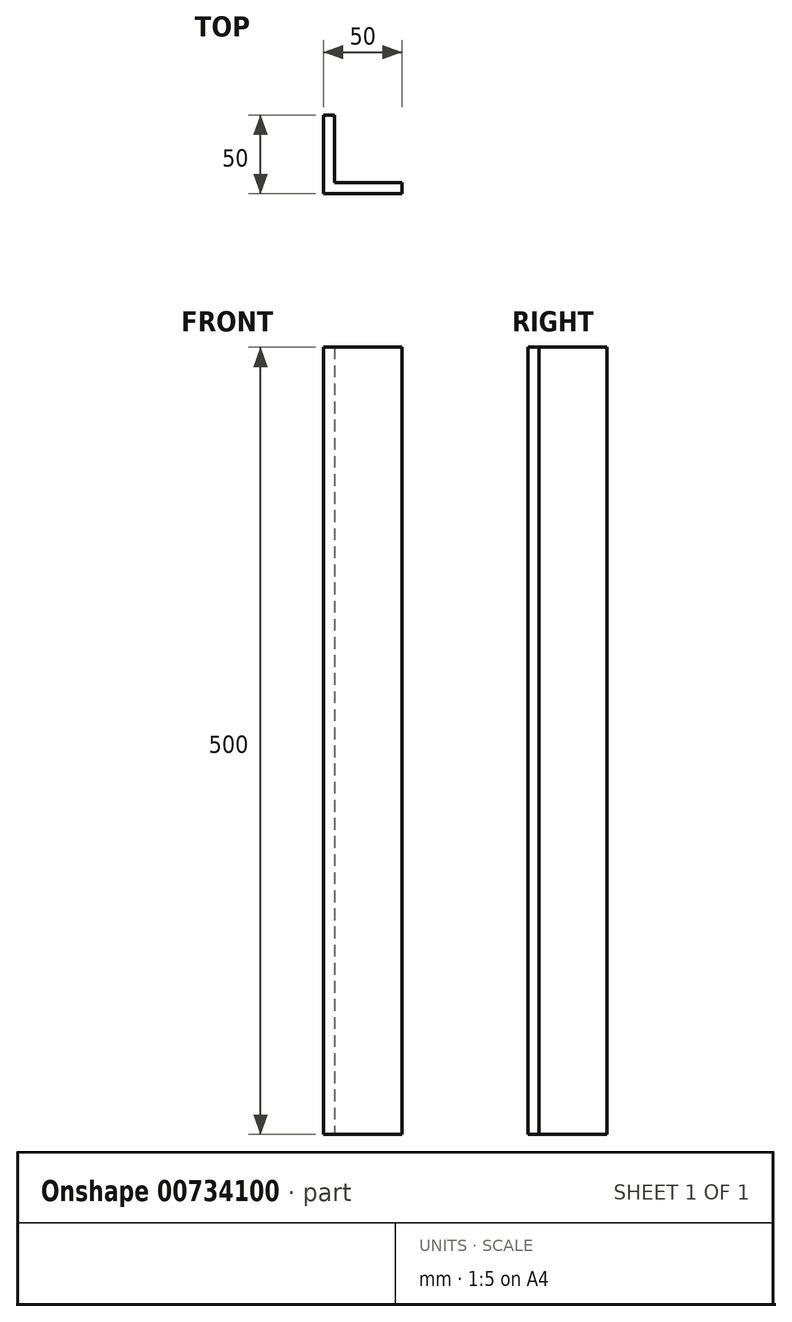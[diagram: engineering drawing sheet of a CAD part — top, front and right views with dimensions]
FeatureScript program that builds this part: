
annotation { "Feature Type Name" : "Feature", "Feature Type Description" : "" }
export const myFeature = defineFeature(function(context is Context, id is Id, definition is map)
    precondition{}
    {
        {
            var Q0;
            Q0=qCreatedBy(makeId("Top.planeOp"),FACE);
            var sketch = newSketch(context, id + "F0", { "sketchPlane" : qUnion([Q0])});
            skLineSegment(sketch, "E0", {"start": v(0, 0) * mm, "end": v(0, -50) * mm});
            skLineSegment(sketch, "E1", {"start": v(0, -50) * mm, "end": v(50, -50) * mm});
            skLineSegment(sketch, "E2", {"start": v(50, -50) * mm, "end": v(50, -43) * mm});
            skLineSegment(sketch, "E3", {"start": v(0, 0) * mm, "end": v(7, 0) * mm});
            skLineSegment(sketch, "E4", {"start": v(7, 0) * mm, "end": v(7, -43) * mm});
            skLineSegment(sketch, "E5", {"start": v(50, -43) * mm, "end": v(7, -43) * mm});
            skSolve(sketch);
        }
        {
            var Q0;
            Q0=makeQuery(id+"F0.imprint","IMPRINT",FACE,{"disambiguationData":[TD([[makeQuery(id+"F0.imprint","IMPRINT",EDGE,{"derivedFrom":sQuery(id+"F0.wireOp",EDGE,"E0")}),1.0]])]});
            extrude(context, id + "F1", {"entities" : qUnion([Q0]), "depth" : 500 * mm, "offsetDistance" : 25 * mm});
        }
    });
